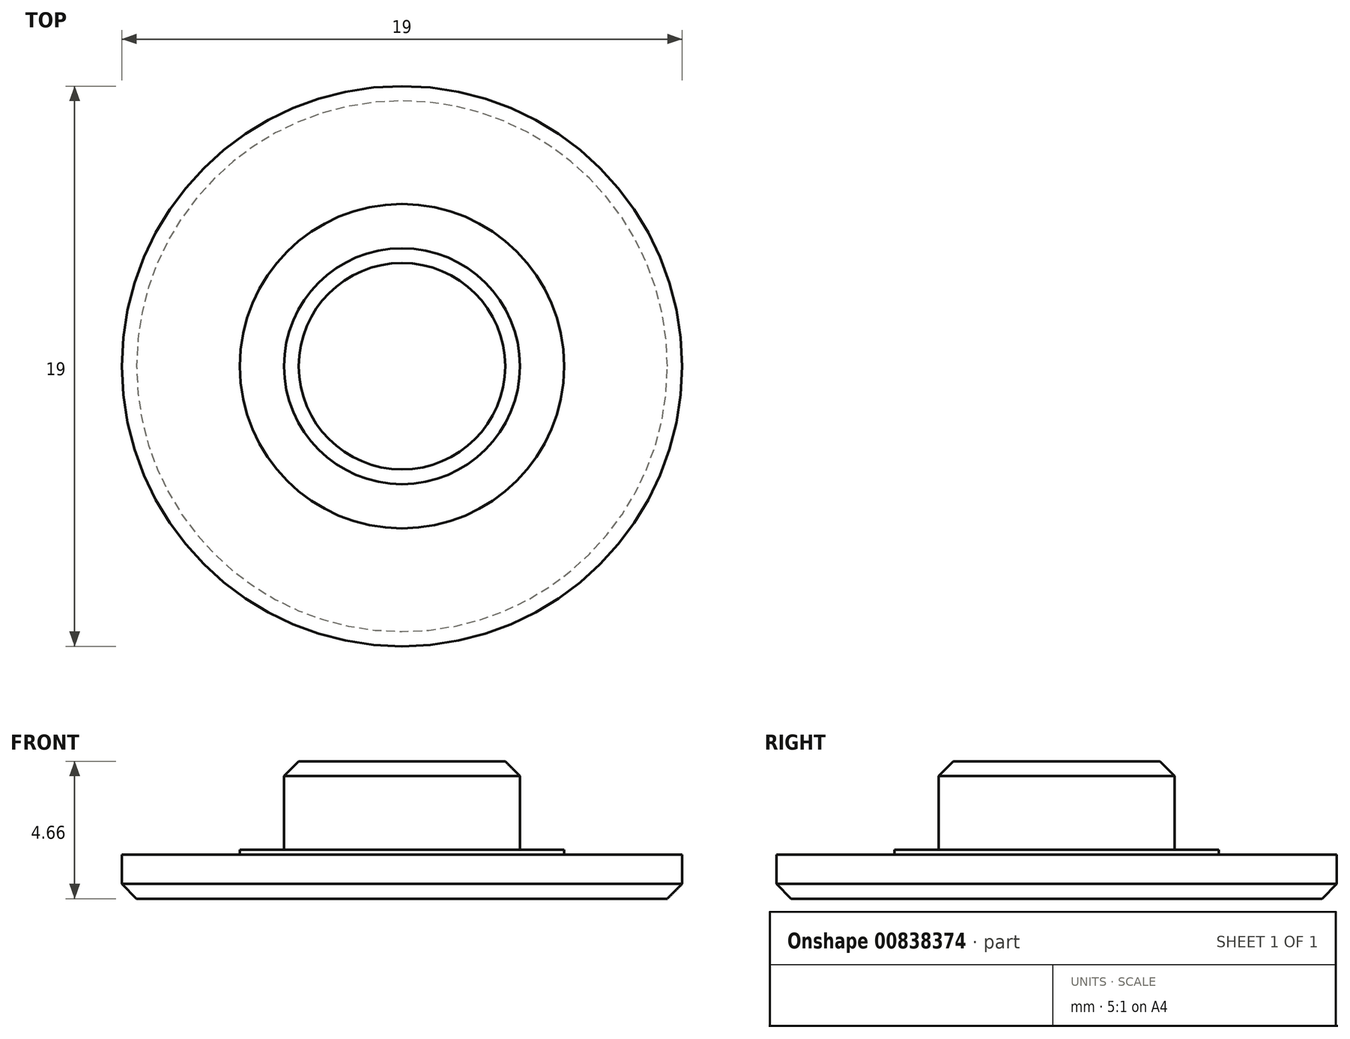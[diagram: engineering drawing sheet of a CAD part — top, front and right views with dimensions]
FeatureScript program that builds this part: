
annotation { "Feature Type Name" : "Feature", "Feature Type Description" : "" }
export const myFeature = defineFeature(function(context is Context, id is Id, definition is map)
    precondition{}
    {
        {
            var Q0;
            Q0=qCreatedBy(makeId("Top.planeOp"),FACE);
            var sketch = newSketch(context, id + "F0", { "sketchPlane" : qUnion([Q0])});
            skCircle(sketch, "E0", {"center": v(0, 0) * mm, "radius": 9.5 * mm});
            skSolve(sketch);
        }
        {
            var Q0;
            Q0 = qSketchRegion(id + "F0", true);
            extrude(context, id + "F1", {"entities" : qUnion([Q0]), "depth" : 1.5 * mm, "offsetDistance" : 25 * mm});
        }
        {
            var Q0;
            Q0=makeQuery(id+"F1.opExtrude","CAP_FACE",FACE,{"disambiguationData":[OSD([sQuery(id+"F0.wireOp",EDGE,"E0")])],"isStart":false});
            var sketch = newSketch(context, id + "F2", { "sketchPlane" : qUnion([Q0])});
            skCircle(sketch, "E1", {"center": v(0, 0) * mm, "radius": 5.5 * mm});
            skSolve(sketch);
        }
        {
            var Q0;
            Q0 = qSketchRegion(id + "F2", true);
            extrude(context, id + "F3", {"entities" : qUnion([Q0]), "operationType" : NewBodyOperationType.ADD, "depth" : 0.16 * mm, "offsetDistance" : 25 * mm});
        }
        {
            var Q0;
            Q0=makeQuery(id+"F3.opExtrude","CAP_FACE",FACE,{"disambiguationData":[OSD([sQuery(id+"F2.wireOp",EDGE,"E1")])],"isStart":false});
            var sketch = newSketch(context, id + "F4", { "sketchPlane" : qUnion([Q0])});
            skCircle(sketch, "E2", {"center": v(0, 0) * mm, "radius": 4 * mm});
            skSolve(sketch);
        }
        {
            var Q0;
            Q0 = qSketchRegion(id + "F4", true);
            extrude(context, id + "F5", {"entities" : qUnion([Q0]), "operationType" : NewBodyOperationType.ADD, "depth" : 3 * mm, "offsetDistance" : 25 * mm});
        }
        {
            var Q0;
            Q0=makeQuery(id+"F5.opExtrude","CAP_EDGE",EDGE,{"disambiguationData":[OSD([sQuery(id+"F4.wireOp",EDGE,"E2")])],"isStart":false});
            chamfer(context, id + "F6", {"entities" : qUnion([Q0]), "width" : 0.5 * mm, "tangentPropagation" : true});
        }
        {
            var Q0;
            Q0=makeQuery(id+"F1.opExtrude","CAP_EDGE",EDGE,{"disambiguationData":[OSD([sQuery(id+"F0.wireOp",EDGE,"E0")])],"isStart":true});
            chamfer(context, id + "F7", {"entities" : qUnion([Q0]), "width" : 0.5 * mm, "tangentPropagation" : true});
        }
    });
